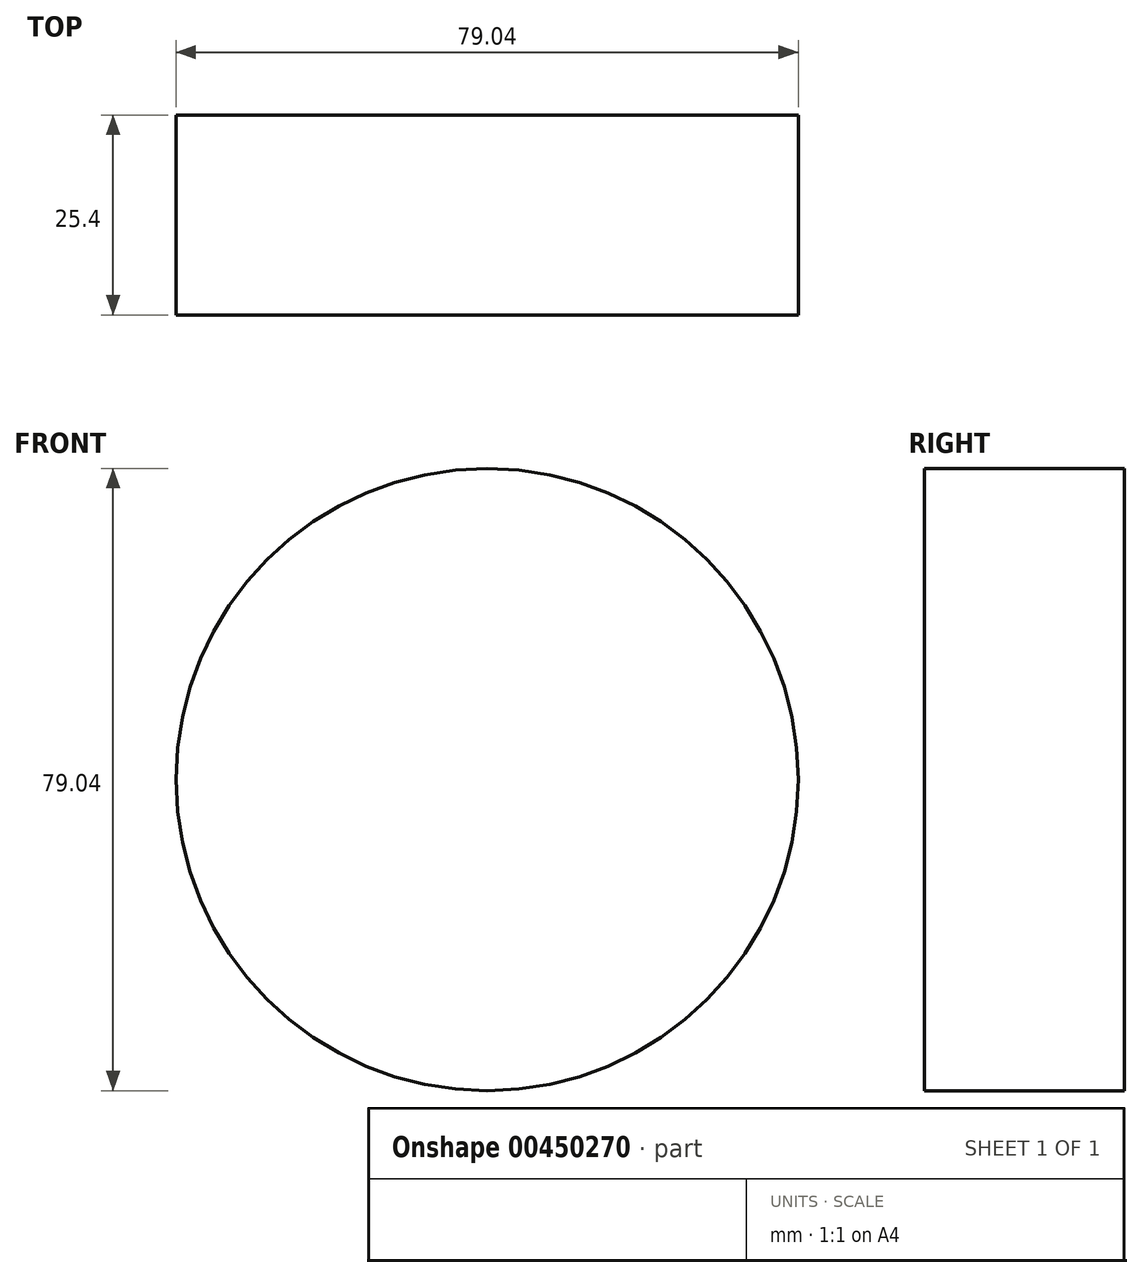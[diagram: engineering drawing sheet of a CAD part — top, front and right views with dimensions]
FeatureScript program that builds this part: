
annotation { "Feature Type Name" : "Feature", "Feature Type Description" : "" }
export const myFeature = defineFeature(function(context is Context, id is Id, definition is map)
    precondition{}
    {
        {
            var Q0;
            Q0=qCreatedBy(makeId("Front.planeOp"),FACE);
            var sketch = newSketch(context, id + "F0", { "sketchPlane" : qUnion([Q0])});
            skCircle(sketch, "E0", {"center": v(0, 0) * mm, "radius": 39.52 * mm});
            skSolve(sketch);
        }
        {
            var Q0;
            Q0=makeQuery(id+"F0.imprint","IMPRINT",FACE,{"disambiguationData":[TD([[makeQuery(id+"F0.imprint","IMPRINT",EDGE,{"derivedFrom":sQuery(id+"F0.wireOp",EDGE,"E0")}),1.0]])]});
            extrude(context, id + "F1", {"entities" : qUnion([Q0]), "depth" : 25.4 * mm});
        }
    });
